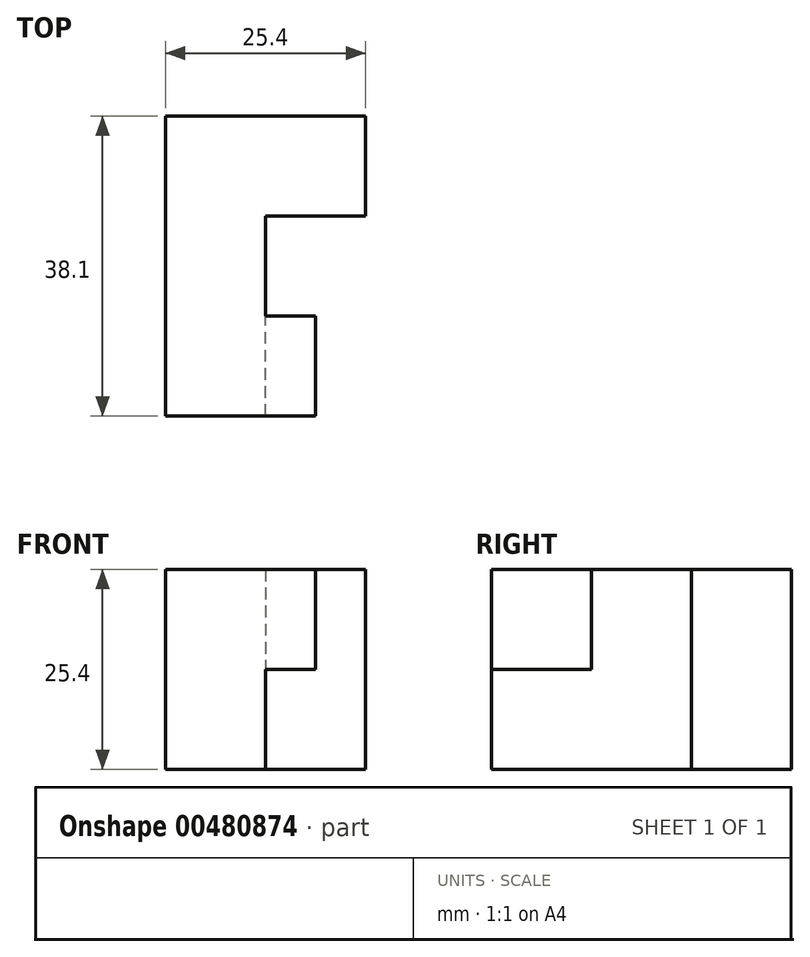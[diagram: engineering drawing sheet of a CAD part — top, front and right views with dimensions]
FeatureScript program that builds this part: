
annotation { "Feature Type Name" : "Feature", "Feature Type Description" : "" }
export const myFeature = defineFeature(function(context is Context, id is Id, definition is map)
    precondition{}
    {
        {
            var Q0;
            Q0=qCreatedBy(makeId("Right.planeOp"),FACE);
            var sketch = newSketch(context, id + "F0", { "sketchPlane" : qUnion([Q0])});
            skLineSegment(sketch, "E0.bottom", {"start": v(37.04, 27.91) * mm, "end": v(-1.06, 27.91) * mm});
            skLineSegment(sketch, "E0.top", {"start": v(37.04, 2.51) * mm, "end": v(-1.06, 2.51) * mm});
            skLineSegment(sketch, "E0.left", {"start": v(37.04, 27.91) * mm, "end": v(37.04, 2.51) * mm});
            skLineSegment(sketch, "E0.right", {"start": v(-1.06, 27.91) * mm, "end": v(-1.06, 2.51) * mm});
            skSolve(sketch);
        }
        {
            var Q0;
            Q0 = qSketchRegion(id + "F0", true);
            extrude(context, id + "F1", {"entities" : qUnion([Q0]), "depth" : 12.7 * mm});
        }
        {
            var Q0;
            Q0=makeQuery(id+"F1.opExtrude","CAP_FACE",FACE,{"disambiguationData":[OSD([sQuery(id+"F0.wireOp",EDGE,"E0.bottom"),sQuery(id+"F0.wireOp",EDGE,"E0.top"),sQuery(id+"F0.wireOp",EDGE,"E0.left"),sQuery(id+"F0.wireOp",EDGE,"E0.right")])],"isStart":false});
            var sketch = newSketch(context, id + "F2", { "sketchPlane" : qUnion([Q0])});
            skLineSegment(sketch, "E1.bottom", {"start": v(37.04, 27.91) * mm, "end": v(24.34, 27.91) * mm});
            skLineSegment(sketch, "E1.top", {"start": v(37.04, 2.51) * mm, "end": v(24.34, 2.51) * mm});
            skLineSegment(sketch, "E1.left", {"start": v(37.04, 27.91) * mm, "end": v(37.04, 2.51) * mm});
            skLineSegment(sketch, "E1.right", {"start": v(24.34, 27.91) * mm, "end": v(24.34, 2.51) * mm});
            skSolve(sketch);
        }
        {
            var Q0;
            Q0 = qSketchRegion(id + "F2", true);
            extrude(context, id + "F3", {"entities" : qUnion([Q0]), "operationType" : NewBodyOperationType.ADD, "depth" : 12.7 * mm});
        }
        {
            var Q0;
            Q0=makeQuery(id+"F1.opExtrude","CAP_FACE",FACE,{"disambiguationData":[OSD([sQuery(id+"F0.wireOp",EDGE,"E0.bottom"),sQuery(id+"F0.wireOp",EDGE,"E0.top"),sQuery(id+"F0.wireOp",EDGE,"E0.left"),sQuery(id+"F0.wireOp",EDGE,"E0.right")])],"isStart":false});
            var sketch = newSketch(context, id + "F4", { "sketchPlane" : qUnion([Q0])});
            skLineSegment(sketch, "E2.bottom", {"start": v(-1.06, 27.91) * mm, "end": v(11.64, 27.91) * mm});
            skLineSegment(sketch, "E2.top", {"start": v(-1.06, 15.21) * mm, "end": v(11.64, 15.21) * mm});
            skLineSegment(sketch, "E2.left", {"start": v(-1.06, 27.91) * mm, "end": v(-1.06, 15.21) * mm});
            skLineSegment(sketch, "E2.right", {"start": v(11.64, 27.91) * mm, "end": v(11.64, 15.21) * mm});
            skSolve(sketch);
        }
        {
            var Q0;
            Q0=makeQuery(id+"F4.imprint","IMPRINT",FACE,{"disambiguationData":[TD([[makeQuery(id+"F4.imprint","IMPRINT",EDGE,{"derivedFrom":sQuery(id+"F4.wireOp",EDGE,"E2.bottom")}),1.0]])]});
            extrude(context, id + "F5", {"entities" : qUnion([Q0]), "operationType" : NewBodyOperationType.ADD, "depth" : 6.35 * mm});
        }
    });
